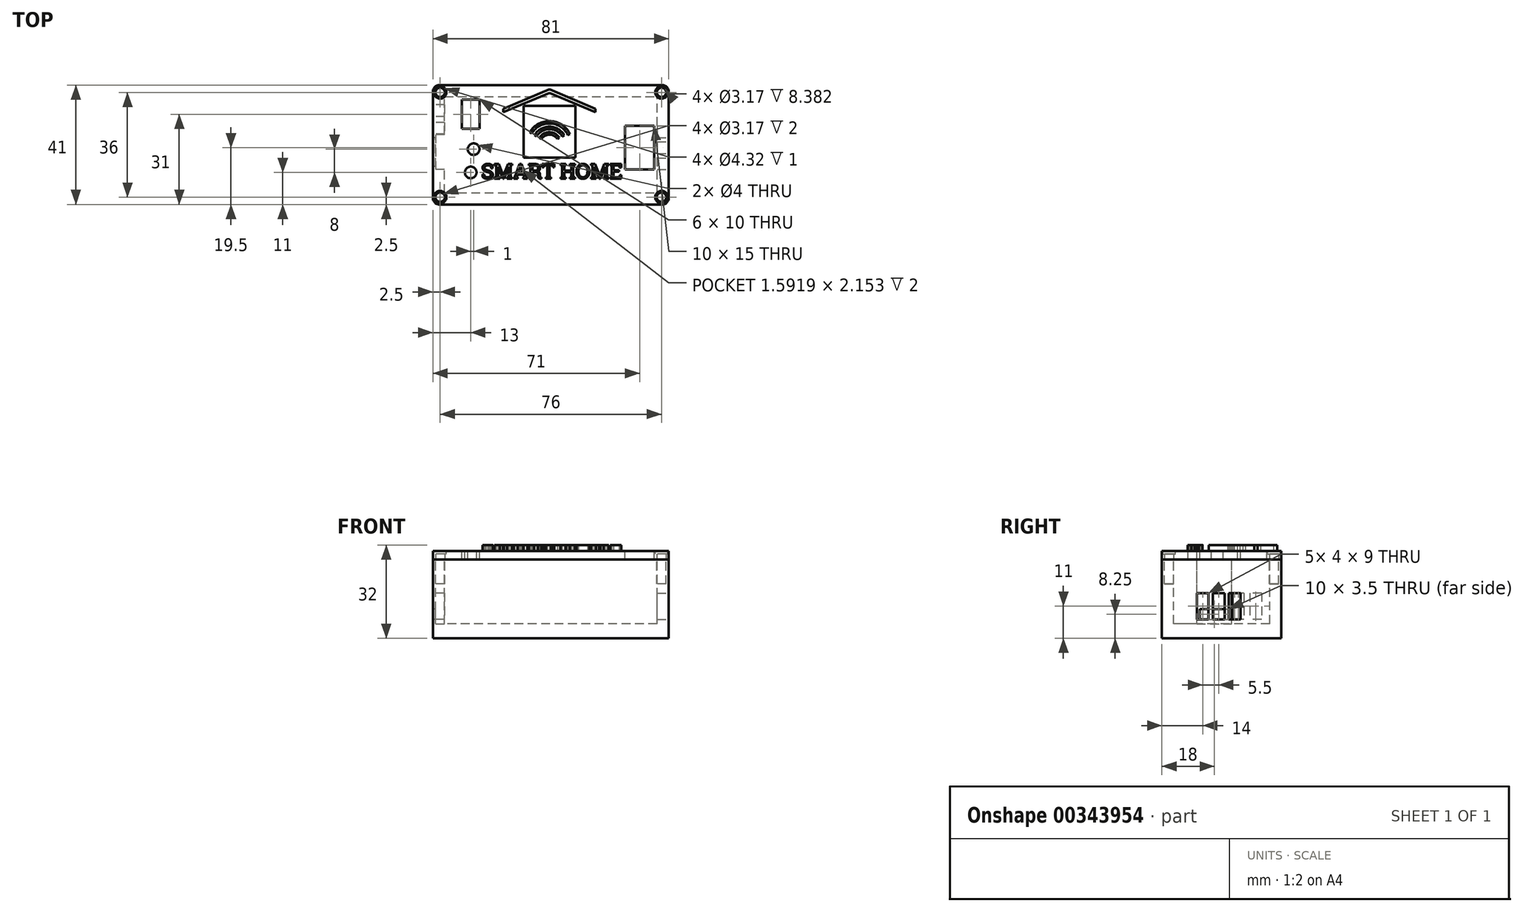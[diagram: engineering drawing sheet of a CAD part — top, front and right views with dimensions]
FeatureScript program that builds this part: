
annotation { "Feature Type Name" : "Feature", "Feature Type Description" : "" }
export const myFeature = defineFeature(function(context is Context, id is Id, definition is map)
    precondition{}
    {
        {
            var Q0;
            Q0=qCreatedBy(makeId("Top.planeOp"),FACE);
            var sketch = newSketch(context, id + "F0", { "sketchPlane" : qUnion([Q0])});
            skLineSegment(sketch, "E0.bottom", {"start": v(0, 0) * mm, "end": v(71, 0) * mm});
            skLineSegment(sketch, "E0.top", {"start": v(0, 31) * mm, "end": v(71, 31) * mm});
            skLineSegment(sketch, "E0.left", {"start": v(0, 0) * mm, "end": v(0, 31) * mm});
            skLineSegment(sketch, "E0.right", {"start": v(71, 0) * mm, "end": v(71, 31) * mm});
            skSolve(sketch);
        }
        {
            var Q0;
            Q0 = qSketchRegion(id + "F0", true);
            extrude(context, id + "F1", {"entities" : qUnion([Q0]), "depth" : 5 * mm});
        }
        {
            var Q0;
            Q0=makeQuery(id+"F1.opExtrude","CAP_FACE",FACE,{"disambiguationData":[OSD([sQuery(id+"F0.wireOp",EDGE,"E0.bottom"),sQuery(id+"F0.wireOp",EDGE,"E0.top"),sQuery(id+"F0.wireOp",EDGE,"E0.left"),sQuery(id+"F0.wireOp",EDGE,"E0.right")])],"isStart":true});
            var sketch = newSketch(context, id + "F2", { "sketchPlane" : qUnion([Q0])});
            skLineSegment(sketch, "E1.0", {"start": v(-5, -36) * mm, "end": v(76, -36) * mm});
            skLineSegment(sketch, "E1.1", {"start": v(-5, 5) * mm, "end": v(-5, -36) * mm});
            skLineSegment(sketch, "E1.2", {"start": v(76, 5) * mm, "end": v(-5, 5) * mm});
            skLineSegment(sketch, "E1.3", {"start": v(76, -36) * mm, "end": v(76, 5) * mm});
            skLineSegment(sketch, "E2.0.0", {"start": v(0, -31) * mm, "end": v(71, -31) * mm});
            skLineSegment(sketch, "E2.0.1", {"start": v(71, -31) * mm, "end": v(71, 0) * mm});
            skLineSegment(sketch, "E2.0.2", {"start": v(71, 0) * mm, "end": v(0, 0) * mm});
            skLineSegment(sketch, "E2.0.3", {"start": v(0, 0) * mm, "end": v(0, -31) * mm});
            skSolve(sketch);
        }
        {
            var Q0;
            Q0 = qSketchRegion(id + "F2", true);
            extrude(context, id + "F3", {"entities" : qUnion([Q0]), "operationType" : NewBodyOperationType.ADD, "oppositeDirection" : true, "depth" : 27 * mm});
        }
        {
            var Q0;
            Q0=qCreatedBy(makeId("Top.planeOp"),FACE);
            var sketch = newSketch(context, id + "F4", { "sketchPlane" : qUnion([Q0])});
            skCircle(sketch, "E3", {"center": v(3, 26) * mm, "radius": 1.5 * mm});
            skCircle(sketch, "E4", {"center": v(3, 4) * mm, "radius": 1.5 * mm});
            skCircle(sketch, "E5", {"center": v(68, 26) * mm, "radius": 1.5 * mm});
            skCircle(sketch, "E6", {"center": v(68, 3.5) * mm, "radius": 1.5 * mm});
            skSolve(sketch);
        }
        {
            var Q0;
            Q0 = qSketchRegion(id + "F4", true);
            extrude(context, id + "F5", {"entities" : qUnion([Q0]), "operationType" : NewBodyOperationType.ADD, "depth" : 6.5 * mm});
        }
        {
            var Q0;
            Q0=makeQuery(id+"F3.opExtrude","CAP_FACE",FACE,{"disambiguationData":[OSD([sQuery(id+"F2.wireOp",EDGE,"E1.0"),sQuery(id+"F2.wireOp",EDGE,"E1.1"),sQuery(id+"F2.wireOp",EDGE,"E1.2"),sQuery(id+"F2.wireOp",EDGE,"E1.3"),sQuery(id+"F2.wireOp",EDGE,"E2.0.0"),sQuery(id+"F2.wireOp",EDGE,"E2.0.1"),sQuery(id+"F2.wireOp",EDGE,"E2.0.2"),sQuery(id+"F2.wireOp",EDGE,"E2.0.3")])],"isStart":false});
            var sketch = newSketch(context, id + "F6", { "sketchPlane" : qUnion([Q0])});
            skLineSegment(sketch, "E7.bottom", {"start": v(0, 18) * mm, "end": v(-3, 18) * mm});
            skLineSegment(sketch, "E7.top", {"start": v(0, 8) * mm, "end": v(-3, 8) * mm});
            skLineSegment(sketch, "E7.left", {"start": v(0, 18) * mm, "end": v(0, 8) * mm});
            skLineSegment(sketch, "E7.right", {"start": v(-3, 18) * mm, "end": v(-3, 8) * mm});
            skSolve(sketch);
        }
        {
            var Q0;
            Q0 = qSketchRegion(id + "F6", true);
            var Q1;
            Q1=makeQuery(id+"F1.opExtrude","CAP_FACE",FACE,{"disambiguationData":[OSD([sQuery(id+"F0.wireOp",EDGE,"E0.bottom"),sQuery(id+"F0.wireOp",EDGE,"E0.top"),sQuery(id+"F0.wireOp",EDGE,"E0.left"),sQuery(id+"F0.wireOp",EDGE,"E0.right")])],"isStart":false});
            extrude(context, id + "F7", {"entities" : qUnion([Q0]), "operationType" : NewBodyOperationType.REMOVE, "endBound" : BoundingType.UP_TO_SURFACE, "oppositeDirection" : true, "endBoundEntityFace" : qUnion([Q1]), "depth" : 21.92 * mm});
        }
        {
            var Q0;
            Q0=makeQuery(id+"F3.opExtrude","SWEPT_FACE",FACE,{"disambiguationData":[OSD([sQuery(id+"F2.wireOp",EDGE,"E1.1")])]});
            var sketch = newSketch(context, id + "F8", { "sketchPlane" : qUnion([Q0])});
            skLineSegment(sketch, "E8.0.1", {"start": v(-18, 6.5) * mm, "end": v(-18, 10) * mm});
            skLineSegment(sketch, "E8.0.3", {"start": v(-8, 10) * mm, "end": v(-8, 6.5) * mm});
            skLineSegment(sketch, "E9.bottom", {"start": v(-18, 6.5) * mm, "end": v(-8, 6.5) * mm});
            skLineSegment(sketch, "E9.top", {"start": v(-18, 10) * mm, "end": v(-8, 10) * mm});
            skLineSegment(sketch, "E9.right", {"start": v(-8, 6.5) * mm, "end": v(-8, 10) * mm});
            skPoint(sketch, "E10.orphan", {"position": v(-8, 5) * mm});
            skPoint(sketch, "E11.orphan", {"position": v(-18, 5) * mm});
            skLineSegment(sketch, "E12", {"start": v(-18, 6.5) * mm, "end": v(-36, 6.5) * mm, "construction": true});
            skPoint(sketch, "E8.0.2.end.orphan", {"position": v(-8, 27) * mm});
            skPoint(sketch, "E8.0.2.start.orphan", {"position": v(-18, 27) * mm});
            skLineSegment(sketch, "E13.bottom", {"start": v(-31, 6.5) * mm, "end": v(-21, 6.5) * mm});
            skLineSegment(sketch, "E13.top", {"start": v(-31, 15.5) * mm, "end": v(-21, 15.5) * mm});
            skLineSegment(sketch, "E13.left", {"start": v(-31, 6.5) * mm, "end": v(-31, 15.5) * mm});
            skLineSegment(sketch, "E13.right", {"start": v(-21, 6.5) * mm, "end": v(-21, 15.5) * mm});
            skSolve(sketch);
        }
        {
            var Q0;
            Q0 = qSketchRegion(id + "F8", true);
            var Q1;
            {var subQ4=sQuery(id+"F2.wireOp",EDGE,"E2.0.0");var subQ5=sQuery(id+"F2.wireOp",EDGE,"E2.0.3");Q1=makeQuery(id+"F7.boolean.opBoolean","SPLIT",FACE,{"disambiguationData":[TD([makeQuery(id+"F3.opExtrude","SWEPT_FACE",FACE,{"disambiguationData":[OSD([subQ4])]})])],"derivedFrom":makeQuery(id+"F3.opExtrude","SWEPT_FACE",FACE,{"disambiguationData":[OSD([subQ5])]})});}
            extrude(context, id + "F9", {"entities" : qUnion([Q0]), "operationType" : NewBodyOperationType.REMOVE, "endBound" : BoundingType.UP_TO_SURFACE, "oppositeDirection" : true, "endBoundEntityFace" : qUnion([Q1]), "depth" : 25.4 * mm});
        }
        {
            var Q0;
            Q0=makeQuery(id+"F3.opExtrude","SWEPT_FACE",FACE,{"disambiguationData":[OSD([sQuery(id+"F2.wireOp",EDGE,"E1.3")])]});
            var sketch = newSketch(context, id + "F10", { "sketchPlane" : qUnion([Q0])});
            skSolve(sketch);
        }
        {
            var Q0;
            Q0=makeQuery(id+"F9.boolean.opBoolean","COPY",FACE,{"derivedFrom":makeQuery(id+"F9.opExtrude","SWEPT_FACE",FACE,{"disambiguationData":[OSD([sQuery(id+"F8.wireOp",EDGE,"E13.bottom")])]})});
            var sketch = newSketch(context, id + "F11", { "sketchPlane" : qUnion([Q0])});
            skLineSegment(sketch, "E14", {"start": v(0, 26) * mm, "end": v(-5, 26) * mm, "construction": true});
            skLineSegment(sketch, "E15", {"start": v(-5, 26) * mm, "end": v(-5.15, 25.86) * mm, "construction": true});
            skLineSegment(sketch, "E16.bottom", {"start": v(-5, 25) * mm, "end": v(0, 25) * mm});
            skLineSegment(sketch, "E16.top", {"start": v(-5, 27) * mm, "end": v(0, 27) * mm});
            skLineSegment(sketch, "E16.left", {"start": v(-5, 25) * mm, "end": v(-5, 27) * mm});
            skLineSegment(sketch, "E16.right", {"start": v(0, 25) * mm, "end": v(0, 27) * mm});
            skPoint(sketch, "E16.middle", {"position": v(-2.5, 26) * mm});
            skSolve(sketch);
        }
        {
            var Q0;
            Q0 = qSketchRegion(id + "F11", true);
            extrude(context, id + "F12", {"entities" : qUnion([Q0]), "operationType" : NewBodyOperationType.ADD, "depth" : 12.78 * mm});
        }
        {
            var Q0;
            {var subQ0=sQuery(id+"F2.wireOp",EDGE,"E1.3");Q0=makeQuery(id+"F10.imprint","IMPRINT",FACE,{"disambiguationData":[TD([[makeQuery(id+"F10.imprint","IMPRINT",EDGE,{"derivedFrom":makeQuery(id+"F3.opExtrude","CAP_EDGE",EDGE,{"disambiguationData":[OSD([subQ0])],"isStart":true})}),-1.0]])]});}
            var sketch = newSketch(context, id + "F13", { "sketchPlane" : qUnion([Q0])});
            skLineSegment(sketch, "E17", {"start": v(18, 6.5) * mm, "end": v(35.94, 6.5) * mm, "construction": true});
            skLineSegment(sketch, "E18.bottom", {"start": v(7, 6.5) * mm, "end": v(11, 6.5) * mm});
            skLineSegment(sketch, "E18.top", {"start": v(7, 15.5) * mm, "end": v(11, 15.5) * mm});
            skLineSegment(sketch, "E18.left", {"start": v(7, 6.5) * mm, "end": v(7, 15.5) * mm});
            skLineSegment(sketch, "E18.right", {"start": v(22, 6.5) * mm, "end": v(22, 15.5) * mm});
            skLineSegment(sketch, "E19.0", {"start": v(31, 27) * mm, "end": v(31, 5) * mm, "construction": true});
            skLineSegment(sketch, "E20.0", {"start": v(0, 27) * mm, "end": v(0, 5) * mm, "construction": true});
            skLineSegment(sketch, "E21", {"start": v(11, 15.5) * mm, "end": v(11, 6.5) * mm});
            skLineSegment(sketch, "E22", {"start": v(12.5, 15.5) * mm, "end": v(12.5, 6.5) * mm});
            skLineSegment(sketch, "E23", {"start": v(18, 15.5) * mm, "end": v(18, 6.5) * mm});
            skLineSegment(sketch, "E24", {"start": v(16.5, 15.5) * mm, "end": v(16.5, 6.5) * mm});
            skLineSegment(sketch, "E25.trimOffspring", {"start": v(11, 6.5) * mm, "end": v(-5.91, 6.5) * mm, "construction": true});
            skLineSegment(sketch, "E26.trimOffspring", {"start": v(12.5, 15.5) * mm, "end": v(16.5, 15.5) * mm});
            skLineSegment(sketch, "E27.trimOffspring", {"start": v(18, 15.5) * mm, "end": v(22, 15.5) * mm});
            skLineSegment(sketch, "E28.trimOffspring", {"start": v(12.5, 6.5) * mm, "end": v(16.5, 6.5) * mm});
            skLineSegment(sketch, "E29.trimOffspring", {"start": v(18, 6.5) * mm, "end": v(22, 6.5) * mm});
            skSolve(sketch);
        }
        {
            var Q0;
            Q0 = qSketchRegion(id + "F13", true);
            extrude(context, id + "F14", {"entities" : qUnion([Q0]), "operationType" : NewBodyOperationType.REMOVE, "oppositeDirection" : true, "depth" : 25.4 * mm});
        }
        {
            var Q0;
            Q0=makeQuery(id+"F3.opExtrude","CAP_FACE",FACE,{"disambiguationData":[OSD([sQuery(id+"F2.wireOp",EDGE,"E1.0"),sQuery(id+"F2.wireOp",EDGE,"E1.1"),sQuery(id+"F2.wireOp",EDGE,"E1.2"),sQuery(id+"F2.wireOp",EDGE,"E1.3"),sQuery(id+"F2.wireOp",EDGE,"E2.0.0"),sQuery(id+"F2.wireOp",EDGE,"E2.0.1"),sQuery(id+"F2.wireOp",EDGE,"E2.0.2"),sQuery(id+"F2.wireOp",EDGE,"E2.0.3")])],"isStart":false});
            var sketch = newSketch(context, id + "F15", { "sketchPlane" : qUnion([Q0])});
            skLineSegment(sketch, "E30", {"start": v(-5, 36) * mm, "end": v(0, 31) * mm, "construction": true});
            skLineSegment(sketch, "E31", {"start": v(71, 31) * mm, "end": v(76, 36) * mm, "construction": true});
            skLineSegment(sketch, "E32", {"start": v(-5, -5) * mm, "end": v(0, 0) * mm, "construction": true});
            skLineSegment(sketch, "E33", {"start": v(76, -5) * mm, "end": v(71, 0) * mm, "construction": true});
            skCircle(sketch, "E34", {"center": v(-2.5, 33.5) * mm, "radius": 1.59 * mm});
            skCircle(sketch, "E35", {"center": v(73.5, 33.5) * mm, "radius": 1.59 * mm});
            skCircle(sketch, "E36", {"center": v(73.5, -2.5) * mm, "radius": 1.59 * mm});
            skCircle(sketch, "E37", {"center": v(-2.5, -2.5) * mm, "radius": 1.59 * mm});
            skSolve(sketch);
        }
        {
            var Q0;
            Q0 = qSketchRegion(id + "F15", true);
            extrude(context, id + "F16", {"entities" : qUnion([Q0]), "operationType" : NewBodyOperationType.REMOVE, "oppositeDirection" : true, "depth" : 8.38 * mm});
        }
        {
            var Q0;
            Q0=makeQuery(id+"F3.opExtrude","SWEPT_EDGE",EDGE,{"disambiguationData":[OSD([sQuery(id+"F2.wireOp",EDGE,"E1.1"),sQuery(id+"F2.wireOp",EDGE,"E1.2")])]});
            var Q1;
            Q1=makeQuery(id+"F3.opExtrude","SWEPT_EDGE",EDGE,{"disambiguationData":[OSD([sQuery(id+"F2.wireOp",EDGE,"E1.0"),sQuery(id+"F2.wireOp",EDGE,"E1.1")])]});
            var Q2;
            Q2=makeQuery(id+"F3.opExtrude","SWEPT_EDGE",EDGE,{"disambiguationData":[OSD([sQuery(id+"F2.wireOp",EDGE,"E1.0"),sQuery(id+"F2.wireOp",EDGE,"E1.3")])]});
            var Q3;
            Q3=makeQuery(id+"F3.opExtrude","SWEPT_EDGE",EDGE,{"disambiguationData":[OSD([sQuery(id+"F2.wireOp",EDGE,"E1.2"),sQuery(id+"F2.wireOp",EDGE,"E1.3")])]});
            fillet(context, id + "F17", {"entities" : qUnion([Q0, Q1, Q2, Q3]), "radius" : 2.27 * mm, "tangentPropagation" : true, "allowEdgeOverflow" : false});
        }
        {
            var Q0;
            Q0=makeQuery(id+"F3.opExtrude","CAP_FACE",FACE,{"disambiguationData":[OSD([sQuery(id+"F2.wireOp",EDGE,"E1.0"),sQuery(id+"F2.wireOp",EDGE,"E1.1"),sQuery(id+"F2.wireOp",EDGE,"E1.2"),sQuery(id+"F2.wireOp",EDGE,"E1.3"),sQuery(id+"F2.wireOp",EDGE,"E2.0.0"),sQuery(id+"F2.wireOp",EDGE,"E2.0.1"),sQuery(id+"F2.wireOp",EDGE,"E2.0.2"),sQuery(id+"F2.wireOp",EDGE,"E2.0.3")])],"isStart":false});
            var sketch = newSketch(context, id + "F18", { "sketchPlane" : qUnion([Q0])});
            skLineSegment(sketch, "E38.0", {"start": v(73.73, -5) * mm, "end": v(-2.73, -5) * mm});
            skArc(sketch, "E39.0", {"start": v(-5, -2.73) * mm, "mid": v(-4.34, -4.34) * mm, "end": v(-2.73, -5) * mm});
            skLineSegment(sketch, "E40.0", {"start": v(-5, -2.73) * mm, "end": v(-5, 33.73) * mm});
            skArc(sketch, "E41.0", {"start": v(-2.73, 36) * mm, "mid": v(-4.34, 35.34) * mm, "end": v(-5, 33.73) * mm});
            skLineSegment(sketch, "E42.0", {"start": v(-2.73, 36) * mm, "end": v(73.73, 36) * mm});
            skArc(sketch, "E43.0", {"start": v(76, 33.73) * mm, "mid": v(75.34, 35.34) * mm, "end": v(73.73, 36) * mm});
            skLineSegment(sketch, "E44.0", {"start": v(76, 33.73) * mm, "end": v(76, -2.73) * mm});
            skArc(sketch, "E45.0", {"start": v(73.73, -5) * mm, "mid": v(75.34, -4.34) * mm, "end": v(76, -2.73) * mm});
            skLineSegment(sketch, "E46.0.0", {"start": v(-2.73, -5) * mm, "end": v(73.73, -5) * mm});
            skCircle(sketch, "E47.0", {"center": v(-2.5, 33.5) * mm, "radius": 1.59 * mm});
            skCircle(sketch, "E48.0", {"center": v(-2.5, -2.5) * mm, "radius": 1.59 * mm});
            skCircle(sketch, "E49.0", {"center": v(73.5, -2.5) * mm, "radius": 1.59 * mm});
            skCircle(sketch, "E50.0", {"center": v(73.5, 33.5) * mm, "radius": 1.59 * mm});
            skSolve(sketch);
        }
        {
            var Q0;
            Q0 = qSketchRegion(id + "F18", true);
            extrude(context, id + "F19", {"entities" : qUnion([Q0]), "depth" : 3 * mm});
        }
        {
            var Q0;
            Q0=makeQuery(id+"F19.opExtrude","CAP_FACE",FACE,{"disambiguationData":[OSD([sQuery(id+"F18.wireOp",EDGE,"E39.0"),sQuery(id+"F18.wireOp",EDGE,"E40.0"),sQuery(id+"F18.wireOp",EDGE,"E41.0"),sQuery(id+"F18.wireOp",EDGE,"E42.0"),sQuery(id+"F18.wireOp",EDGE,"E43.0"),sQuery(id+"F18.wireOp",EDGE,"E44.0"),sQuery(id+"F18.wireOp",EDGE,"E45.0"),sQuery(id+"F18.wireOp",EDGE,"E38.0"),sQuery(id+"F18.wireOp",EDGE,"E47.0"),sQuery(id+"F18.wireOp",EDGE,"E48.0"),sQuery(id+"F18.wireOp",EDGE,"E49.0"),sQuery(id+"F18.wireOp",EDGE,"E50.0")])],"isStart":false});
            var sketch = newSketch(context, id + "F20", { "sketchPlane" : qUnion([Q0])});
            skCircle(sketch, "E51", {"center": v(-2.5, 33.5) * mm, "radius": 2.16 * mm});
            skCircle(sketch, "E52", {"center": v(-2.5, -2.5) * mm, "radius": 2.16 * mm});
            skCircle(sketch, "E53", {"center": v(73.5, -2.5) * mm, "radius": 2.16 * mm});
            skCircle(sketch, "E54", {"center": v(73.5, 33.5) * mm, "radius": 2.16 * mm});
            skSolve(sketch);
        }
        {
            var Q0;
            Q0 = qSketchRegion(id + "F20", true);
            extrude(context, id + "F21", {"entities" : qUnion([Q0]), "operationType" : NewBodyOperationType.REMOVE, "oppositeDirection" : true, "depth" : 1 * mm});
        }
        {
            var Q0;
            Q0=makeQuery(id+"F19.opExtrude","CAP_FACE",FACE,{"disambiguationData":[OSD([sQuery(id+"F18.wireOp",EDGE,"E39.0"),sQuery(id+"F18.wireOp",EDGE,"E40.0"),sQuery(id+"F18.wireOp",EDGE,"E41.0"),sQuery(id+"F18.wireOp",EDGE,"E42.0"),sQuery(id+"F18.wireOp",EDGE,"E43.0"),sQuery(id+"F18.wireOp",EDGE,"E44.0"),sQuery(id+"F18.wireOp",EDGE,"E45.0"),sQuery(id+"F18.wireOp",EDGE,"E38.0"),sQuery(id+"F18.wireOp",EDGE,"E47.0"),sQuery(id+"F18.wireOp",EDGE,"E48.0"),sQuery(id+"F18.wireOp",EDGE,"E49.0"),sQuery(id+"F18.wireOp",EDGE,"E50.0")])],"isStart":false});
            var sketch = newSketch(context, id + "F22", { "sketchPlane" : qUnion([Q0])});
            skPoint(sketch, "E55.0.start.orphan", {"position": v(0, 18) * mm});
            skPoint(sketch, "E56.0.end.orphan", {"position": v(0, 8) * mm});
            skLineSegment(sketch, "E57", {"start": v(0, 27) * mm, "end": v(0, 25) * mm, "construction": true});
            skLineSegment(sketch, "E58", {"start": v(0, 31) * mm, "end": v(71, 31) * mm, "construction": true});
            skLineSegment(sketch, "E59", {"start": v(71, 31) * mm, "end": v(71, 0) * mm, "construction": true});
            skLineSegment(sketch, "E60", {"start": v(0, 0) * mm, "end": v(71, 0) * mm, "construction": true});
            skLineSegment(sketch, "E61", {"start": v(0, 21) * mm, "end": v(15.06, 21) * mm, "construction": true});
            skLineSegment(sketch, "E62.bottom", {"start": v(5, 21) * mm, "end": v(11, 21) * mm});
            skLineSegment(sketch, "E62.top", {"start": v(5, 31) * mm, "end": v(11, 31) * mm});
            skLineSegment(sketch, "E62.left", {"start": v(5, 21) * mm, "end": v(5, 31) * mm});
            skLineSegment(sketch, "E62.right", {"start": v(11, 21) * mm, "end": v(11, 31) * mm});
            skLineSegment(sketch, "E63.trimOffspring", {"start": v(0, 21) * mm, "end": v(0, 0) * mm, "construction": true});
            skPoint(sketch, "E64.0.end.orphan", {"position": v(0, 31) * mm});
            skLineSegment(sketch, "E65.0", {"start": v(71, 11) * mm, "end": v(71, 7) * mm});
            skLineSegment(sketch, "E66.0", {"start": v(71, 22) * mm, "end": v(71, 18) * mm});
            skLineSegment(sketch, "E67", {"start": v(71, 18) * mm, "end": v(71, 11) * mm});
            skLineSegment(sketch, "E68", {"start": v(71, 22) * mm, "end": v(61, 22) * mm});
            skLineSegment(sketch, "E69", {"start": v(71, 7) * mm, "end": v(61, 7) * mm});
            skLineSegment(sketch, "E70", {"start": v(61, 7) * mm, "end": v(61, 22) * mm});
            skCircle(sketch, "E71", {"center": v(9, 14) * mm, "radius": 2 * mm});
            skCircle(sketch, "E72", {"center": v(8, 6) * mm, "radius": 2 * mm});
            skSolve(sketch);
        }
        {
            var Q0;
            Q0 = qSketchRegion(id + "F22", true);
            extrude(context, id + "F23", {"entities" : qUnion([Q0]), "operationType" : NewBodyOperationType.REMOVE, "oppositeDirection" : true, "depth" : 10.4 * mm});
        }
        {
            var Q0;
            Q0=makeQuery(id+"F19.opExtrude","CAP_FACE",FACE,{"disambiguationData":[OSD([sQuery(id+"F18.wireOp",EDGE,"E39.0"),sQuery(id+"F18.wireOp",EDGE,"E40.0"),sQuery(id+"F18.wireOp",EDGE,"E41.0"),sQuery(id+"F18.wireOp",EDGE,"E42.0"),sQuery(id+"F18.wireOp",EDGE,"E43.0"),sQuery(id+"F18.wireOp",EDGE,"E44.0"),sQuery(id+"F18.wireOp",EDGE,"E45.0"),sQuery(id+"F18.wireOp",EDGE,"E38.0"),sQuery(id+"F18.wireOp",EDGE,"E47.0"),sQuery(id+"F18.wireOp",EDGE,"E48.0"),sQuery(id+"F18.wireOp",EDGE,"E49.0"),sQuery(id+"F18.wireOp",EDGE,"E50.0")])],"isStart":false});
            var sketch = newSketch(context, id + "F24", { "sketchPlane" : qUnion([Q0])});
            skText(sketch, "E73", { "text": "SMART HOME", "fontName": "RobotoSlab-Regular.ttf"});
            skLineSegment(sketch, "E74.bottom", {"start": v(27.7, 12.62) * mm, "end": v(42.32, 12.62) * mm});
            skLineSegment(sketch, "E74.top", {"start": v(27.7, 27.25) * mm, "end": v(42.32, 27.25) * mm});
            skLineSegment(sketch, "E74.left", {"start": v(27.7, 12.62) * mm, "end": v(27.7, 27.25) * mm});
            skLineSegment(sketch, "E74.right", {"start": v(42.32, 12.62) * mm, "end": v(42.32, 27.25) * mm});
            skLineSegment(sketch, "E75.0", {"start": v(43.9, 11.04) * mm, "end": v(43.9, 28.82) * mm});
            skLineSegment(sketch, "E75.1", {"start": v(26.12, 11.04) * mm, "end": v(43.9, 11.04) * mm});
            skLineSegment(sketch, "E75.2", {"start": v(26.12, 11.04) * mm, "end": v(26.12, 28.82) * mm});
            skLineSegment(sketch, "E75.3", {"start": v(26.12, 28.82) * mm, "end": v(43.9, 28.82) * mm});
            skLineSegment(sketch, "E76", {"start": v(35, 33.34) * mm, "end": v(19.16, 26.65) * mm});
            skPoint(sketch, "E76.startSnap0", {"position": v(35, 28.82) * mm});
            skLineSegment(sketch, "E77", {"start": v(35, 28.82) * mm, "end": v(35, 35.06) * mm, "construction": true});
            skLineSegment(sketch, "E78.0", {"start": v(35, 34.53) * mm, "end": v(19.16, 27.83) * mm});
            skLineSegment(sketch, "E79", {"start": v(19.16, 26.65) * mm, "end": v(19.16, 27.83) * mm});
            skLineSegment(sketch, "E80.MirrorCS", {"start": v(35, 33.34) * mm, "end": v(50.85, 26.65) * mm});
            skLineSegment(sketch, "E81.MirrorCS", {"start": v(35, 34.53) * mm, "end": v(50.85, 27.83) * mm});
            skLineSegment(sketch, "E82.MirrorCS", {"start": v(50.85, 26.65) * mm, "end": v(50.85, 27.83) * mm});
            skCircle(sketch, "E83", {"center": v(35, 15.8) * mm, "radius": 1.56 * mm});
            skArc(sketch, "E84", {"start": v(31.62, 17.95) * mm, "mid": v(34.97, 19.81) * mm, "end": v(38.36, 18) * mm});
            skArc(sketch, "E85", {"start": v(29.95, 18.87) * mm, "mid": v(35.07, 21.72) * mm, "end": v(40.12, 18.76) * mm});
            skArc(sketch, "E86.0", {"start": v(32.3, 17.51) * mm, "mid": v(34.98, 19) * mm, "end": v(37.68, 17.56) * mm});
            skArc(sketch, "E87.0", {"start": v(30.65, 18.45) * mm, "mid": v(35.06, 20.9) * mm, "end": v(39.42, 18.35) * mm});
            skLineSegment(sketch, "E88", {"start": v(29.95, 18.87) * mm, "end": v(30.65, 18.45) * mm});
            skLineSegment(sketch, "E89", {"start": v(31.62, 17.95) * mm, "end": v(32.3, 17.51) * mm});
            skLineSegment(sketch, "E90", {"start": v(37.68, 17.56) * mm, "end": v(38.36, 18) * mm});
            skLineSegment(sketch, "E91", {"start": v(39.42, 18.35) * mm, "end": v(40.12, 18.76) * mm});
            skArc(sketch, "E92", {"start": v(29, 19.44) * mm, "mid": v(35.33, 22.82) * mm, "end": v(41.33, 18.87) * mm});
            skArc(sketch, "E93.0", {"start": v(28.3, 19.86) * mm, "mid": v(35.37, 23.63) * mm, "end": v(42.06, 19.22) * mm});
            skLineSegment(sketch, "E94", {"start": v(28.3, 19.86) * mm, "end": v(29, 19.44) * mm});
            skLineSegment(sketch, "E95", {"start": v(41.33, 18.87) * mm, "end": v(42.06, 19.22) * mm});
            const initialGuessF24  = {"E73": [0.01164, 0.00388, 1, 0, 0.00508]};
            skSetInitialGuess(sketch, initialGuessF24);
            skSolve(sketch);
        }
        {
            var Q0;
            Q0 = qSketchRegion(id + "F24", true);
            var Q1;
            Q1=makeQuery(id+"F24.imprint","IMPRINT",FACE,{"disambiguationData":[TD([[makeQuery(id+"F24.imprint","IMPRINT",EDGE,{"derivedFrom":sQuery(id+"F24.wireOp",EDGE,"E83")}),1.0]])]});
            var Q2;
            Q2=makeQuery(id+"F24.imprint","IMPRINT",FACE,{"disambiguationData":[TD([[makeQuery(id+"F24.imprint","IMPRINT",EDGE,{"derivedFrom":sQuery(id+"F24.wireOp",EDGE,"E84")}),-1.0]])]});
            var Q3;
            Q3=makeQuery(id+"F24.imprint","IMPRINT",FACE,{"disambiguationData":[TD([[makeQuery(id+"F24.imprint","IMPRINT",EDGE,{"derivedFrom":sQuery(id+"F24.wireOp",EDGE,"E85")}),-1.0]])]});
            var Q4;
            Q4=makeQuery(id+"F24.imprint","IMPRINT",FACE,{"disambiguationData":[TD([[makeQuery(id+"F24.imprint","IMPRINT",EDGE,{"derivedFrom":sQuery(id+"F24.wireOp",EDGE,"E92")}),1.0]])]});
            extrude(context, id + "F25", {"entities" : qUnion([Q0, Q1, Q2, Q3, Q4]), "operationType" : NewBodyOperationType.ADD, "depth" : 2 * mm});
        }
        {
            var Q0;
            Q0=makeQuery(id+"F3.opExtrude","CAP_FACE",FACE,{"disambiguationData":[OSD([sQuery(id+"F2.wireOp",EDGE,"E1.0"),sQuery(id+"F2.wireOp",EDGE,"E1.1"),sQuery(id+"F2.wireOp",EDGE,"E1.2"),sQuery(id+"F2.wireOp",EDGE,"E1.3"),sQuery(id+"F2.wireOp",EDGE,"E2.0.0"),sQuery(id+"F2.wireOp",EDGE,"E2.0.1"),sQuery(id+"F2.wireOp",EDGE,"E2.0.2"),sQuery(id+"F2.wireOp",EDGE,"E2.0.3")])],"isStart":false});
            var sketch = newSketch(context, id + "F26", { "sketchPlane" : qUnion([Q0])});
            skLineSegment(sketch, "E96.0", {"start": v(-1, 19) * mm, "end": v(-4, 19) * mm});
            skLineSegment(sketch, "E96.1", {"start": v(-4, 19) * mm, "end": v(-4, 7) * mm});
            skLineSegment(sketch, "E96.2", {"start": v(-1, 19) * mm, "end": v(-1, 32) * mm});
            skLineSegment(sketch, "E96.3", {"start": v(-1, 7) * mm, "end": v(-4, 7) * mm});
            skLineSegment(sketch, "E96.4", {"start": v(-1, 32) * mm, "end": v(72, 32) * mm});
            skLineSegment(sketch, "E96.5", {"start": v(72, -1) * mm, "end": v(72, 32) * mm});
            skLineSegment(sketch, "E96.6", {"start": v(-1, -1) * mm, "end": v(72, -1) * mm});
            skLineSegment(sketch, "E96.7", {"start": v(-1, -1) * mm, "end": v(-1, 7) * mm});
            skSolve(sketch);
        }
        {
            var Q0;
            Q0 = qSketchRegion(id + "F26", true);
            var Q1;
            {var subQ0=sQuery(id+"F0.wireOp",EDGE,"E0.right");var subQ1=sQuery(id+"F0.wireOp",EDGE,"E0.left");var subQ2=sQuery(id+"F0.wireOp",EDGE,"E0.top");var subQ3=sQuery(id+"F0.wireOp",EDGE,"E0.bottom");Q1=makeQuery(id+"F7.boolean.opBoolean","MERGE",FACE,{"derivedFrom":[makeQuery(id+"F1.opExtrude","CAP_FACE",FACE,{"disambiguationData":[OSD([subQ3,subQ2,subQ1,subQ0])],"isStart":false}),makeQuery(id+"F7.opExtrude","CAP_FACE",FACE,{"disambiguationData":[OSD([subQ3,subQ2,subQ1,subQ0])],"isStart":false})]});}
            extrude(context, id + "F27", {"entities" : qUnion([Q0]), "operationType" : NewBodyOperationType.REMOVE, "endBound" : BoundingType.UP_TO_SURFACE, "oppositeDirection" : true, "endBoundEntityFace" : qUnion([Q1]), "depth" : 25.4 * mm});
        }
        {
            var Q0;
            Q0=makeQuery(id+"F12.boolean.opBoolean","MERGE",FACE,{"derivedFrom":[makeQuery(id+"F3.opExtrude","SWEPT_FACE",FACE,{"disambiguationData":[OSD([sQuery(id+"F2.wireOp",EDGE,"E1.1")])]}),makeQuery(id+"F12.opExtrude","SWEPT_FACE",FACE,{"disambiguationData":[OSD([sQuery(id+"F11.wireOp",EDGE,"E16.left")])]})]});
            var sketch = newSketch(context, id + "F28", { "sketchPlane" : qUnion([Q0])});
            skLineSegment(sketch, "E97.bottom", {"start": v(-31, 15.5) * mm, "end": v(-29.2, 15.5) * mm});
            skLineSegment(sketch, "E97.top", {"start": v(-31, 6.5) * mm, "end": v(-29.2, 6.5) * mm});
            skLineSegment(sketch, "E97.left", {"start": v(-31, 15.5) * mm, "end": v(-31, 6.5) * mm});
            skLineSegment(sketch, "E97.right", {"start": v(-29.2, 15.5) * mm, "end": v(-29.2, 6.5) * mm});
            skLineSegment(sketch, "E98.bottom", {"start": v(-25, 15.5) * mm, "end": v(-23.2, 15.5) * mm});
            skLineSegment(sketch, "E98.top", {"start": v(-25, 6.5) * mm, "end": v(-23.2, 6.5) * mm});
            skLineSegment(sketch, "E98.left", {"start": v(-25, 15.5) * mm, "end": v(-25, 6.5) * mm});
            skLineSegment(sketch, "E98.right", {"start": v(-23.2, 15.5) * mm, "end": v(-23.2, 6.5) * mm});
            skSolve(sketch);
        }
        {
            var Q0;
            Q0 = qSketchRegion(id + "F28", true);
            var Q1;
            Q1=makeQuery(id+"F27.boolean.opBoolean","COPY",FACE,{"derivedFrom":makeQuery(id+"F27.opExtrude","SWEPT_FACE",FACE,{"disambiguationData":[OSD([sQuery(id+"F26.wireOp",EDGE,"E96.2")])]})});
            extrude(context, id + "F29", {"entities" : qUnion([Q0]), "operationType" : NewBodyOperationType.ADD, "endBound" : BoundingType.UP_TO_SURFACE, "oppositeDirection" : true, "endBoundEntityFace" : qUnion([Q1]), "depth" : 25.4 * mm});
        }
        {
            var Q0;
            Q0=makeQuery(id+"F29.boolean.opBoolean","MERGE",FACE,{"derivedFrom":[makeQuery(id+"F12.boolean.opBoolean","MERGE",FACE,{"derivedFrom":[makeQuery(id+"F3.opExtrude","SWEPT_FACE",FACE,{"disambiguationData":[OSD([sQuery(id+"F2.wireOp",EDGE,"E1.1")])]}),makeQuery(id+"F12.opExtrude","SWEPT_FACE",FACE,{"disambiguationData":[OSD([sQuery(id+"F11.wireOp",EDGE,"E16.left")])]})]}),makeQuery(id+"F29.opExtrude","CAP_FACE",FACE,{"disambiguationData":[OSD([sQuery(id+"F28.wireOp",EDGE,"E97.bottom"),sQuery(id+"F28.wireOp",EDGE,"E97.top"),sQuery(id+"F28.wireOp",EDGE,"E97.left"),sQuery(id+"F28.wireOp",EDGE,"E97.right")])],"isStart":true}),makeQuery(id+"F29.opExtrude","CAP_FACE",FACE,{"disambiguationData":[OSD([sQuery(id+"F28.wireOp",EDGE,"E98.bottom"),sQuery(id+"F28.wireOp",EDGE,"E98.top"),sQuery(id+"F28.wireOp",EDGE,"E98.left"),sQuery(id+"F28.wireOp",EDGE,"E98.right")])],"isStart":true})]});
            var sketch = newSketch(context, id + "F30", { "sketchPlane" : qUnion([Q0])});
            skLineSegment(sketch, "E99.bottom", {"start": v(-27, 15.5) * mm, "end": v(-25.2, 15.5) * mm});
            skLineSegment(sketch, "E99.top", {"start": v(-27, 6.5) * mm, "end": v(-25.2, 6.5) * mm});
            skLineSegment(sketch, "E99.left", {"start": v(-27, 15.5) * mm, "end": v(-27, 6.5) * mm});
            skLineSegment(sketch, "E99.right", {"start": v(-25.2, 15.5) * mm, "end": v(-25.2, 6.5) * mm});
            skLineSegment(sketch, "E100.bottom", {"start": v(-21, 15.5) * mm, "end": v(-19.2, 15.5) * mm});
            skLineSegment(sketch, "E100.top", {"start": v(-21, 6.5) * mm, "end": v(-19.2, 6.5) * mm});
            skLineSegment(sketch, "E100.left", {"start": v(-21, 15.5) * mm, "end": v(-21, 6.5) * mm});
            skLineSegment(sketch, "E100.right", {"start": v(-19.2, 15.5) * mm, "end": v(-19.2, 6.5) * mm});
            skSolve(sketch);
        }
        {
            var Q0;
            Q0 = qSketchRegion(id + "F30", true);
            var Q1;
            {var subQ0=sQuery(id+"F26.wireOp",EDGE,"E96.2");Q1=makeQuery(id+"F29.boolean.opBoolean","MERGE",FACE,{"derivedFrom":[makeQuery(id+"F27.boolean.opBoolean","COPY",FACE,{"derivedFrom":makeQuery(id+"F27.opExtrude","SWEPT_FACE",FACE,{"disambiguationData":[OSD([subQ0])]})}),makeQuery(id+"F29.opExtrude","CAP_FACE",FACE,{"disambiguationData":[OSD([subQ0]),ownerDisambiguation([makeQuery(id+"F28.imprint","IMPRINT",EDGE,{"derivedFrom":sQuery(id+"F28.wireOp",EDGE,"E97.bottom")})])],"isStart":false}),makeQuery(id+"F29.opExtrude","CAP_FACE",FACE,{"disambiguationData":[OSD([subQ0]),ownerDisambiguation([makeQuery(id+"F28.imprint","IMPRINT",EDGE,{"derivedFrom":sQuery(id+"F28.wireOp",EDGE,"E98.bottom")})])],"isStart":false})]});}
            extrude(context, id + "F31", {"entities" : qUnion([Q0]), "operationType" : NewBodyOperationType.REMOVE, "endBound" : BoundingType.UP_TO_SURFACE, "oppositeDirection" : true, "endBoundEntityFace" : qUnion([Q1]), "depth" : 25.4 * mm});
        }
    });
